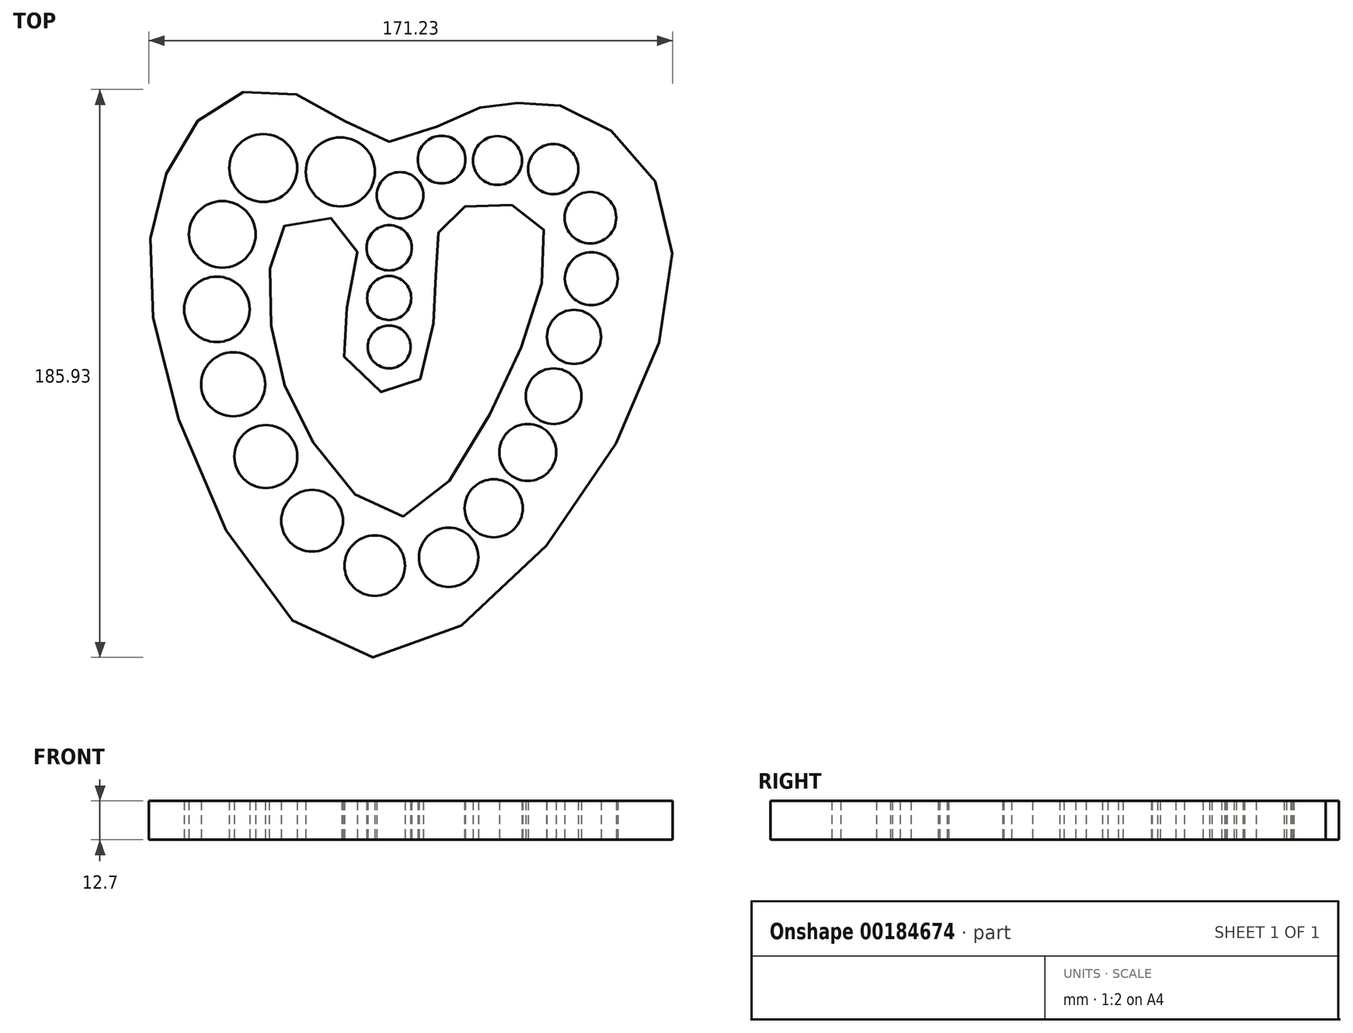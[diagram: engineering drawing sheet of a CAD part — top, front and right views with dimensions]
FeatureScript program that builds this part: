
annotation { "Feature Type Name" : "Feature", "Feature Type Description" : "" }
export const myFeature = defineFeature(function(context is Context, id is Id, definition is map)
    precondition{}
    {
        {
            var Q0;
            Q0=qCreatedBy(makeId("Top.planeOp"),FACE);
            var sketch = newSketch(context, id + "F0", { "sketchPlane" : qUnion([Q0])});
            skCircle(sketch, "E0", {"center": v(-54.58, 43.14) * mm, "radius": 10.9 * mm});
            skCircle(sketch, "E1", {"center": v(-51.03, -5.93) * mm, "radius": 10.5 * mm});
            skCircle(sketch, "E2", {"center": v(-41.2, 64.87) * mm, "radius": 11.1 * mm});
            skCircle(sketch, "E3", {"center": v(-40.35, -29.58) * mm, "radius": 10.3 * mm});
            skCircle(sketch, "E4", {"center": v(0, 22.32) * mm, "radius": 7.2 * mm});
            skCircle(sketch, "E5", {"center": v(65.82, 48.6) * mm, "radius": 8.45 * mm});
            skCircle(sketch, "E6", {"center": v(66.11, 28.65) * mm, "radius": 8.65 * mm});
            skCircle(sketch, "E7", {"center": v(-56.35, 18.61) * mm, "radius": 10.7 * mm});
            skCircle(sketch, "E8", {"center": v(60.46, 9.6) * mm, "radius": 8.85 * mm});
            skCircle(sketch, "E9", {"center": v(3.56, 55.94) * mm, "radius": 7.6 * mm});
            skCircle(sketch, "E10", {"center": v(53.67, 64.52) * mm, "radius": 8.22 * mm});
            skCircle(sketch, "E11", {"center": v(17.15, 67.64) * mm, "radius": 7.8 * mm});
            skCircle(sketch, "E12", {"center": v(-25.21, -50.56) * mm, "radius": 10.1 * mm});
            skCircle(sketch, "E13", {"center": v(45.33, -28.23) * mm, "radius": 9.3 * mm});
            skCircle(sketch, "E14", {"center": v(35.41, 67.33) * mm, "radius": 8 * mm});
            skCircle(sketch, "E15", {"center": v(53.8, -9.81) * mm, "radius": 9.1 * mm});
            skCircle(sketch, "E16", {"center": v(0, 6.31) * mm, "radius": 7 * mm});
            skCircle(sketch, "E17", {"center": v(0, 38.75) * mm, "radius": 7.4 * mm});
            skCircle(sketch, "E18", {"center": v(-4.7, -65.3) * mm, "radius": 9.9 * mm});
            skCircle(sketch, "E19", {"center": v(34.18, -46.51) * mm, "radius": 9.5 * mm});
            skCircle(sketch, "E20", {"center": v(19.46, -62.57) * mm, "radius": 9.7 * mm});
            skCircle(sketch, "E21", {"center": v(-15.96, 63.6) * mm, "radius": 11.3 * mm});
            skSolve(sketch);
        }
        {
            var Q0;
            Q0=qCreatedBy(makeId("Top.planeOp"),FACE);
            var sketch = newSketch(context, id + "F1", { "sketchPlane" : qUnion([Q0])});
            skFitSpline(sketch, "E22", {"points": [v(0, 73.47) * mm, v(-23.82, 86.26) * mm, v(-51.96, 88.3) * mm, v(-73.45, 61.7) * mm, v(-73.97, 0) * mm, v(-10.52, -94.87) * mm, v(76.54, -20.95) * mm, v(87.94, 58.49) * mm, v(58.36, 84.6) * mm, v(39.58, 85.95) * mm, v(24.28, 82.85) * mm, v(0, 73.47) * mm]});
            skFitSpline(sketch, "E23", {"points": [v(4.55, -49.22) * mm, v(30.77, -19.72) * mm, v(49.04, 23.36) * mm, v(49.04, 47.71) * mm, v(33.11, 53.33) * mm, v(18.13, 48.18) * mm, v(15.32, 33.67) * mm, v(14.38, 13.53) * mm, v(5.48, -8.95) * mm, v(-13.25, 0) * mm, v(-13.25, 21.5) * mm, v(-12.78, 44.9) * mm, v(-32.45, 47.25) * mm, v(-39, 31.32) * mm, v(-36.2, 0) * mm, v(-19.34, -32.83) * mm, v(4.55, -49.22) * mm]});
            skSolve(sketch);
        }
        {
            var Q0;
            Q0=makeQuery(id+"F1.imprint","IMPRINT",FACE,{"disambiguationData":[TD([[makeQuery(id+"F1.imprint","IMPRINT",EDGE,{"derivedFrom":sQuery(id+"F1.wireOp",EDGE,"E22")}),1.0]])]});
            var Q1;
            Q1=sQuery(id+"F1.wireOp",EDGE,"E23");
            var Q2;
            Q2=sQuery(id+"F1.wireOp",EDGE,"E22");
            extrude(context, id + "F2", {"entities" : qUnion([Q0]), "surfaceEntities" : qUnion([Q1, Q2]), "endBound" : BoundingType.SYMMETRIC, "depth" : 12.7 * mm});
        }
        {
            var Q0;
            Q0 = qSketchRegion(id + "F0", true);
            extrude(context, id + "F3", {"entities" : qUnion([Q0]), "operationType" : NewBodyOperationType.REMOVE, "depth" : 25.4 * mm});
        }
        {
            var Q0;
            Q0 = qSketchRegion(id + "F0", true);
            extrude(context, id + "F4", {"entities" : qUnion([Q0]), "operationType" : NewBodyOperationType.REMOVE, "oppositeDirection" : true, "depth" : 25.4 * mm});
        }
    });
